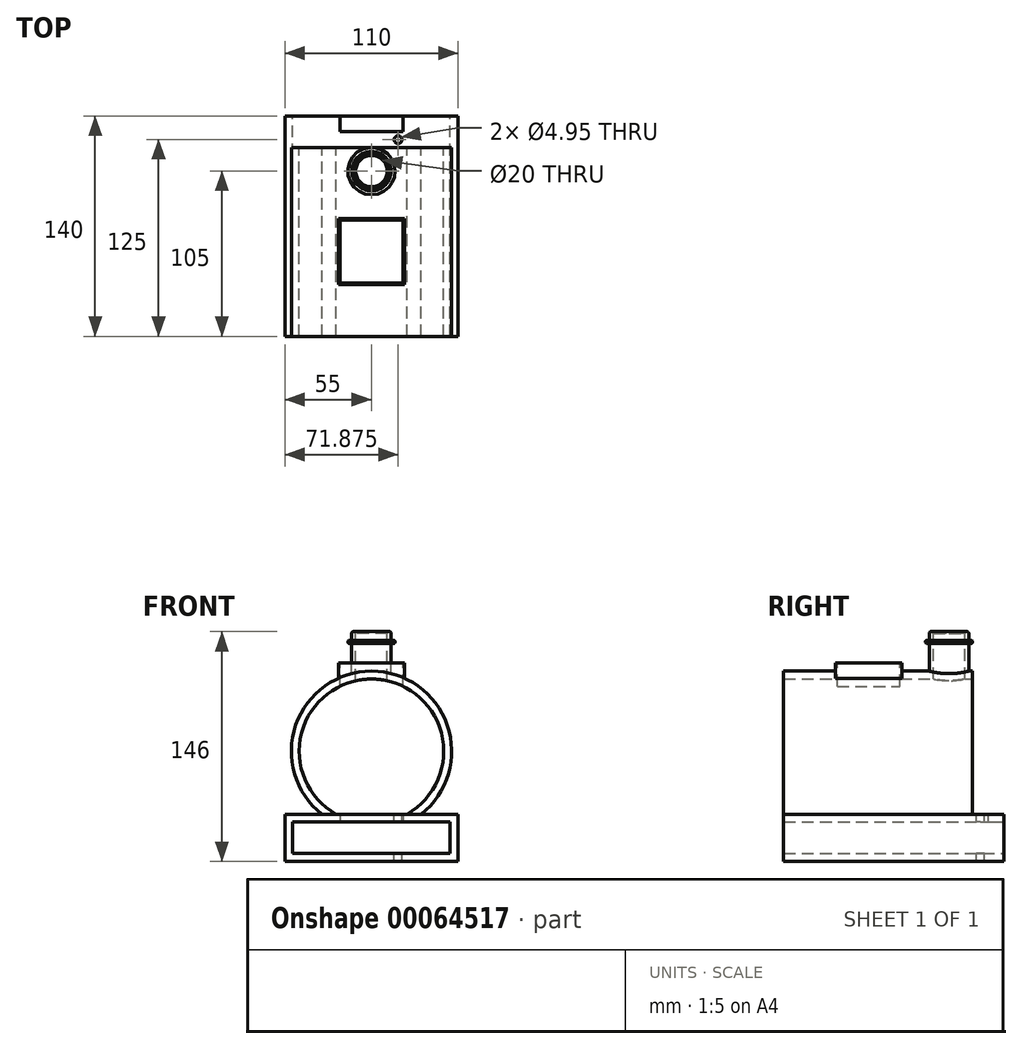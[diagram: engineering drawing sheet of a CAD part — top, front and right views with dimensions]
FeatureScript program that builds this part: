
annotation { "Feature Type Name" : "Feature", "Feature Type Description" : "" }
export const myFeature = defineFeature(function(context is Context, id is Id, definition is map)
    precondition{}
    {
        {
            var Q0;
            Q0=qCreatedBy(makeId("Front.planeOp"),FACE);
            var sketch = newSketch(context, id + "F0", { "sketchPlane" : qUnion([Q0])});
            skCircle(sketch, "E0", {"center": v(0, 0) * mm, "radius": 45.9 * mm});
            skLineSegment(sketch, "E1", {"start": v(-22.5, -40) * mm, "end": v(22.5, -40) * mm});
            skPoint(sketch, "E2", {"position": v(0, -40) * mm});
            skCircle(sketch, "E3", {"center": v(0, 0) * mm, "radius": 50.9 * mm});
            skLineSegment(sketch, "E4", {"start": v(-55, -40) * mm, "end": v(-22.5, -40) * mm});
            skLineSegment(sketch, "E5", {"start": v(0, -40) * mm, "end": v(22.5, -40) * mm});
            skLineSegment(sketch, "E6", {"start": v(22.5, -40) * mm, "end": v(55, -40) * mm});
            skLineSegment(sketch, "E7", {"start": v(55, -40) * mm, "end": v(55, -70) * mm});
            skLineSegment(sketch, "E8", {"start": v(55, -70) * mm, "end": v(-55, -70) * mm});
            skLineSegment(sketch, "E9", {"start": v(-55, -70) * mm, "end": v(-55, -40) * mm});
            skPoint(sketch, "E10", {"position": v(0, -54.83) * mm});
            skPoint(sketch, "E11", {"position": v(0, -45.9) * mm});
            skPoint(sketch, "E12", {"position": v(0, -50.9) * mm});
            skPoint(sketch, "E13", {"position": v(7.73, -70) * mm});
            skLineSegment(sketch, "E14", {"start": v(-50.9, 0) * mm, "end": v(-45.9, 0) * mm});
            skLineSegment(sketch, "E15", {"start": v(-45.9, 0) * mm, "end": v(-17, 0) * mm});
            skLineSegment(sketch, "E16", {"start": v(-17, 0) * mm, "end": v(0, 0) * mm});
            skLineSegment(sketch, "E17", {"start": v(0, 0) * mm, "end": v(17, 0) * mm});
            skLineSegment(sketch, "E18", {"start": v(17, 0) * mm, "end": v(45.9, 0) * mm});
            skLineSegment(sketch, "E19", {"start": v(45.9, 0) * mm, "end": v(50.9, 0) * mm});
            skCircle(sketch, "E20", {"center": v(0, 0) * mm, "radius": 40 * mm});
            skLineSegment(sketch, "E21.bottom", {"start": v(50, -45) * mm, "end": v(-50, -45) * mm});
            skLineSegment(sketch, "E21.top", {"start": v(50, -65) * mm, "end": v(-50, -65) * mm});
            skLineSegment(sketch, "E21.left", {"start": v(50, -45) * mm, "end": v(50, -65) * mm});
            skLineSegment(sketch, "E21.right", {"start": v(-50, -45) * mm, "end": v(-50, -65) * mm});
            skLineSegment(sketch, "E22", {"start": v(-50, -40) * mm, "end": v(-50, -45) * mm, "construction": true});
            skLineSegment(sketch, "E23", {"start": v(-50, -45) * mm, "end": v(-55, -45) * mm, "construction": true});
            skLineSegment(sketch, "E24", {"start": v(55, -45) * mm, "end": v(50, -45) * mm, "construction": true});
            skLineSegment(sketch, "E25", {"start": v(50, -45) * mm, "end": v(50, -40) * mm, "construction": true});
            skPoint(sketch, "E26", {"position": v(0, 40) * mm});
            skPoint(sketch, "E27", {"position": v(0, 45.9) * mm});
            skPoint(sketch, "E28", {"position": v(0, 50.9) * mm});
            skLineSegment(sketch, "E29", {"start": v(-50, -65) * mm, "end": v(-55, -65) * mm});
            skLineSegment(sketch, "E30", {"start": v(-50, -65) * mm, "end": v(-50, -70) * mm});
            skSolve(sketch);
        }
        {
            var Q0;
            {var subQ3=sQuery(id+"F0.wireOp",EDGE,"E14");Q0=makeQuery(id+"F0.imprint","IMPRINT",FACE,{"disambiguationData":[TD([[makeQuery(id+"F0.imprint","IMPRINT",EDGE,{"derivedFrom":subQ3}),-1.0]])]});}
            var Q1;
            {var subQ3=sQuery(id+"F0.wireOp",EDGE,"E19");Q1=makeQuery(id+"F0.imprint","IMPRINT",FACE,{"disambiguationData":[TD([[makeQuery(id+"F0.imprint","IMPRINT",EDGE,{"derivedFrom":subQ3}),-1.0]])]});}
            var Q2;
            {var subQ0=sQuery(id+"F0.wireOp",EDGE,"E14");Q2=makeQuery(id+"F0.imprint","IMPRINT",FACE,{"disambiguationData":[TD([[makeQuery(id+"F0.imprint","IMPRINT",EDGE,{"derivedFrom":subQ0}),1.0]])]});}
            extrude(context, id + "F1", {"entities" : qUnion([Q0, Q1, Q2]), "depth" : 120 * mm});
        }
        {
            var Q0;
            {var subQ0=sQuery(id+"F0.wireOp",EDGE,"E6");var subQ5=sQuery(id+"F0.wireOp",EDGE,"E3");var subQ7=makeQuery(id+"F0.imprint","INTERSECT",VERTEX,{"derivedFrom":[subQ5,subQ0]});Q0=makeQuery(id+"F0.imprint","IMPRINT",FACE,{"disambiguationData":[TD([[makeQuery(id+"F0.imprint","IMPRINT",EDGE,{"disambiguationData":[TD([[subQ7,1.0]])],"derivedFrom":subQ5}),1.0]])]});}
            var Q1;
            {var subQ1=sQuery(id+"F0.wireOp",EDGE,"E1");Q1=makeQuery(id+"F0.imprint","IMPRINT",FACE,{"disambiguationData":[TD([[makeQuery(id+"F0.imprint","IMPRINT",EDGE,{"derivedFrom":subQ1}),-1.0]])]});}
            var Q2;
            {var subQ0=sQuery(id+"F0.wireOp",EDGE,"E4");var subQ5=sQuery(id+"F0.wireOp",EDGE,"E3");var subQ6=makeQuery(id+"F0.imprint","INTERSECT",VERTEX,{"derivedFrom":[subQ5,subQ0]});Q2=makeQuery(id+"F0.imprint","IMPRINT",FACE,{"disambiguationData":[TD([[makeQuery(id+"F0.imprint","IMPRINT",EDGE,{"disambiguationData":[TD([[subQ6,-1.0]])],"derivedFrom":subQ5}),1.0]])]});}
            var Q3;
            {var subQ0=sQuery(id+"F0.wireOp",EDGE,"E21.right");Q3=makeQuery(id+"F0.imprint","IMPRINT",FACE,{"disambiguationData":[TD([[makeQuery(id+"F0.imprint","IMPRINT",EDGE,{"derivedFrom":subQ0}),-1.0]])]});}
            var Q4;
            {var subQ4=sQuery(id+"F0.wireOp",EDGE,"E29");Q4=makeQuery(id+"F0.imprint","IMPRINT",FACE,{"disambiguationData":[TD([[makeQuery(id+"F0.imprint","IMPRINT",EDGE,{"derivedFrom":subQ4}),1.0]])]});}
            var Q5;
            {var subQ1=sQuery(id+"F0.wireOp",EDGE,"E7");Q5=makeQuery(id+"F0.imprint","IMPRINT",FACE,{"disambiguationData":[TD([[makeQuery(id+"F0.imprint","IMPRINT",EDGE,{"derivedFrom":subQ1}),-1.0]])]});}
            extrude(context, id + "F2", {"entities" : qUnion([Q0, Q1, Q2, Q3, Q4, Q5]), "depth" : 120 * mm, "hasSecondDirection" : true, "secondDirectionOppositeDirection" : true, "secondDirectionDepth" : 20 * mm});
        }
        {
            var Q0;
            Q0=qCreatedBy(makeId("Top.planeOp"),FACE);
            var Q1;
            Q1=sQuery(id+"F0.wireOp",VERTEX,"E27");
            cPlane(context, id + "F3", {"entities" : qUnion([Q0, Q1]), "cplaneType" : CPlaneType.PLANE_POINT, "offset" : 50 * mm, "width" : 150 * mm, "height" : 150 * mm});
        }
        {
            var Q0;
            Q0=qCreatedBy(makeId("Top.planeOp"),FACE);
            cPlane(context, id + "F4", {"entities" : qUnion([Q0]), "cplaneType" : CPlaneType.OFFSET, "offset" : 56 * mm, "width" : 150 * mm, "height" : 150 * mm});
        }
        {
            var Q0;
            Q0=qCreatedBy(id+"F4.planeOp",FACE);
            cPlane(context, id + "F5", {"entities" : qUnion([Q0]), "cplaneType" : CPlaneType.OFFSET, "offset" : 20 * mm, "width" : 150 * mm, "height" : 150 * mm});
        }
        {
            var Q0;
            Q0=qCreatedBy(id+"F5.planeOp",FACE);
            var sketch = newSketch(context, id + "F6", { "sketchPlane" : qUnion([Q0])});
            skCircle(sketch, "E31", {"center": v(0, -15) * mm, "radius": 10 * mm});
            skCircle(sketch, "E32", {"center": v(0, -15) * mm, "radius": 12.5 * mm});
            skSolve(sketch);
        }
        {
            var Q0;
            Q0=makeQuery(id+"F6.imprint","IMPRINT",FACE,{"disambiguationData":[TD([[makeQuery(id+"F6.imprint","IMPRINT",EDGE,{"derivedFrom":sQuery(id+"F6.wireOp",EDGE,"E31")}),-1.0]])]});
            extrude(context, id + "F7", {"entities" : qUnion([Q0]), "operationType" : NewBodyOperationType.ADD, "oppositeDirection" : true, "depth" : 30 * mm});
        }
        {
            var Q0;
            Q0=qCreatedBy(id+"F4.planeOp",FACE);
            var sketch = newSketch(context, id + "F8", { "sketchPlane" : qUnion([Q0])});
            skLineSegment(sketch, "E33.bottom", {"start": v(-50, 0) * mm, "end": v(50, 0) * mm});
            skLineSegment(sketch, "E33.top", {"start": v(-50, -145) * mm, "end": v(50, -145) * mm});
            skLineSegment(sketch, "E33.left", {"start": v(-50, 0) * mm, "end": v(-50, -145) * mm});
            skLineSegment(sketch, "E33.right", {"start": v(50, 0) * mm, "end": v(50, -145) * mm});
            skLineSegment(sketch, "E34.bottom", {"start": v(-21, -45) * mm, "end": v(21, -45) * mm});
            skLineSegment(sketch, "E34.top", {"start": v(-21, -87) * mm, "end": v(21, -87) * mm});
            skLineSegment(sketch, "E34.left", {"start": v(-21, -45) * mm, "end": v(-21, -87) * mm});
            skLineSegment(sketch, "E34.right", {"start": v(21, -45) * mm, "end": v(21, -87) * mm});
            skLineSegment(sketch, "E35.bottom", {"start": v(-20, -46) * mm, "end": v(20, -46) * mm});
            skLineSegment(sketch, "E35.top", {"start": v(-20, -86) * mm, "end": v(20, -86) * mm});
            skLineSegment(sketch, "E35.left", {"start": v(-20, -46) * mm, "end": v(-20, -86) * mm});
            skLineSegment(sketch, "E35.right", {"start": v(20, -46) * mm, "end": v(20, -86) * mm});
            skCircle(sketch, "E36", {"center": v(0, -15) * mm, "radius": 12.5 * mm});
            skCircle(sketch, "E37", {"center": v(0, -15) * mm, "radius": 10 * mm});
            skLineSegment(sketch, "E38", {"start": v(0, -27.5) * mm, "end": v(0, -45) * mm, "construction": true});
            skLineSegment(sketch, "E39", {"start": v(0, -2.5) * mm, "end": v(0, 0) * mm, "construction": true});
            skSolve(sketch);
        }
        {
            var Q0;
            Q0=makeQuery(id+"F8.imprint","IMPRINT",FACE,{"disambiguationData":[TD([[makeQuery(id+"F8.imprint","IMPRINT",EDGE,{"derivedFrom":sQuery(id+"F8.wireOp",EDGE,"E37")}),1.0]])]});
            extrude(context, id + "F9", {"entities" : qUnion([Q0]), "operationType" : NewBodyOperationType.REMOVE, "oppositeDirection" : true, "depth" : 25 * mm});
        }
        {
            var Q0;
            Q0=makeQuery(id+"F8.imprint","IMPRINT",FACE,{"disambiguationData":[TD([[makeQuery(id+"F8.imprint","IMPRINT",EDGE,{"derivedFrom":sQuery(id+"F8.wireOp",EDGE,"E34.bottom")}),-1.0]])]});
            var Q1;
            Q1=makeQuery(id+"F8.imprint","IMPRINT",FACE,{"disambiguationData":[TD([[makeQuery(id+"F8.imprint","IMPRINT",EDGE,{"derivedFrom":sQuery(id+"F8.wireOp",EDGE,"73f20b46-5f5b-4ee4-84c1-b2e9693b60b3.bottom")}),-1.0]])]});
            extrude(context, id + "F10", {"entities" : qUnion([Q0, Q1]), "operationType" : NewBodyOperationType.ADD, "oppositeDirection" : true, "depth" : 10 * mm});
        }
        {
            var Q0;
            Q0=makeQuery(id+"F8.imprint","IMPRINT",FACE,{"disambiguationData":[TD([[makeQuery(id+"F8.imprint","IMPRINT",EDGE,{"derivedFrom":sQuery(id+"F8.wireOp",EDGE,"E35.bottom")}),-1.0]])]});
            var Q1;
            Q1=makeQuery(id+"F8.imprint","IMPRINT",FACE,{"disambiguationData":[TD([[makeQuery(id+"F8.imprint","IMPRINT",EDGE,{"derivedFrom":sQuery(id+"F8.wireOp",EDGE,"efbebbf9-9281-459a-8338-6bcefca7b141.bottom")}),-1.0]])]});
            extrude(context, id + "F11", {"entities" : qUnion([Q0, Q1]), "operationType" : NewBodyOperationType.REMOVE, "oppositeDirection" : true, "depth" : 25 * mm});
        }
        {
            var Q0;
            Q0=makeQuery(id+"F2.opExtrude","SWEPT_FACE",FACE,{"disambiguationData":[OSD([sQuery(id+"F0.wireOp",EDGE,"E1"),sQuery(id+"F0.wireOp",EDGE,"E4"),sQuery(id+"F0.wireOp",EDGE,"E5"),sQuery(id+"F0.wireOp",EDGE,"E6")])]});
            var sketch = newSketch(context, id + "F12", { "sketchPlane" : qUnion([Q0])});
            skLineSegment(sketch, "E40.bottom", {"start": v(-20, 50) * mm, "end": v(20, 50) * mm});
            skLineSegment(sketch, "E40.top", {"start": v(-20, 10) * mm, "end": v(20, 10) * mm});
            skLineSegment(sketch, "E40.left", {"start": v(-20, 50) * mm, "end": v(-20, 10) * mm});
            skLineSegment(sketch, "E40.right", {"start": v(20, 50) * mm, "end": v(20, 10) * mm});
            skCircle(sketch, "E41", {"center": v(0, 60) * mm, "radius": 2.44 * mm});
            skCircle(sketch, "E42", {"center": v(16.88, 5) * mm, "radius": 2.48 * mm});
            skLineSegment(sketch, "E43", {"start": v(0, 60) * mm, "end": v(0, 80) * mm, "construction": true});
            skPoint(sketch, "E44.endSnap0", {"position": v(0, 0) * mm});
            skPoint(sketch, "E45", {"position": v(0, 50) * mm});
            skLineSegment(sketch, "E46", {"start": v(0, 50) * mm, "end": v(0, 60) * mm, "construction": true});
            skSolve(sketch);
        }
        {
            var Q0;
            Q0=qSketchRegion(id+"F12",true);
            extrude(context, id + "F13", {"entities" : qUnion([Q0]), "operationType" : NewBodyOperationType.REMOVE, "oppositeDirection" : true, "depth" : 25 * mm});
        }
        {
            var Q0;
            Q0=makeQuery(id+"F12.imprint","IMPRINT",FACE,{"disambiguationData":[TD([[makeQuery(id+"F12.imprint","IMPRINT",EDGE,{"derivedFrom":sQuery(id+"F12.wireOp",EDGE,"E42")}),1.0]])]});
            extrude(context, id + "F14", {"entities" : qUnion([Q0]), "operationType" : NewBodyOperationType.REMOVE, "oppositeDirection" : true, "depth" : 100 * mm});
        }
        {
            var Q0;
            Q0=qCreatedBy(id+"F5.planeOp",FACE);
            cPlane(context, id + "F15", {"entities" : qUnion([Q0]), "cplaneType" : CPlaneType.OFFSET, "offset" : 7.5 * mm, "oppositeDirection" : true, "width" : 150 * mm, "height" : 150 * mm});
        }
        {
            var Q0;
            Q0=qCreatedBy(id+"F15.planeOp",FACE);
            var sketch = newSketch(context, id + "F16", { "sketchPlane" : qUnion([Q0])});
            skCircle(sketch, "E47", {"center": v(0, -15) * mm, "radius": 15 * mm});
            skCircle(sketch, "E48", {"center": v(0, -15) * mm, "radius": 10 * mm});
            skSolve(sketch);
        }
        {
            var Q0;
            Q0=makeQuery(id+"F16.imprint","IMPRINT",FACE,{"disambiguationData":[TD([[makeQuery(id+"F16.imprint","IMPRINT",EDGE,{"derivedFrom":sQuery(id+"F16.wireOp",EDGE,"E47")}),1.0]])]});
            extrude(context, id + "F17", {"entities" : qUnion([Q0]), "operationType" : NewBodyOperationType.ADD, "depth" : 2 * mm});
        }
        {
            var Q0;
            Q0=makeQuery(id+"F17.opExtrude","CAP_EDGE",EDGE,{"disambiguationData":[OSD([sQuery(id+"F16.wireOp",EDGE,"E47")])],"isStart":false});
            var Q1;
            Q1=makeQuery(id+"F17.opExtrude","CAP_EDGE",EDGE,{"disambiguationData":[OSD([sQuery(id+"F16.wireOp",EDGE,"E47")])],"isStart":true});
            var Q2;
            Q2=makeQuery(id+"F7.opExtrude","CAP_EDGE",EDGE,{"disambiguationData":[OSD([sQuery(id+"F6.wireOp",EDGE,"E32")])],"isStart":true});
            fillet(context, id + "F18", {"entities" : qUnion([Q0, Q1, Q2]), "radius" : 1 * mm, "tangentPropagation" : true, "allowEdgeOverflow" : false});
        }
        {
            var Q0;
            Q0=makeQuery(id+"F7.opExtrude","CAP_EDGE",EDGE,{"disambiguationData":[OSD([sQuery(id+"F6.wireOp",EDGE,"E31")])],"isStart":true});
            chamfer(context, id + "F19", {"entities" : qUnion([Q0]), "width" : 1 * mm, "tangentPropagation" : true});
        }
    });
